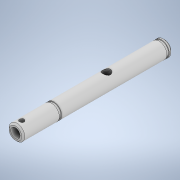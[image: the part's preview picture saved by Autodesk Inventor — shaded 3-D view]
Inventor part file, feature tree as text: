
AUTODESK INVENTOR PART (.ipt)
format: ipt  version: 2022 (Build 260153000, 153)  size: 167,936 bytes
history: native  units: mm
features: sketch x4, extrude x3, thread x2, projected_geometry x2, revolve x1, plane x1
ambient origin geometry x8: Origin, YZ Plane, XZ Plane, XY Plane, X Axis, Y Axis, Z Axis, Center Point
bodies: Solid1 (feature_tree)
feature tree (13):
  revolve  "Revolution1"  [1 undecoded]
  extrude  "Extrusion1"  Depth=1.5mm
  plane  "Work Plane1"
  extrude  "Extrusion2"  Depth=1.5mm
  extrude  "Extrusion3"  TaperAngle=135.0deg  [1 undecoded]
  thread  "Thread1"  [1 undecoded]
  thread  "Thread2"  [1 undecoded]
  sketch  "Sketch1"  dims[d9=95.0mm d10=5.0mm]
  sketch  "Sketch2"  dims[d11=0.5mm d12=1.5mm]
  sketch  "Sketch3"  dims[d13=1.5mm d14=2.0mm]
  projected_geometry  "Projected Loop1"
  sketch  "Sketch4"  dims[d15=1.0mm d16=135.0deg d17=67.0mm d18=135.0deg d19=1.414mm d20=90.0deg d21=6.0mm d22=10.0mm d23=0.0mm d24=5.0mm d25=5.0mm d26=67.0mm d27=33.5mm d28=10.0mm d29=0.0mm d30=3.0mm d31=4.0mm d32=10.0mm d33=0.0mm d34=10.0mm d35=0.0mm d36=10.0mm d37=0.0mm]
  projected_geometry  "Projected Loop2"
note: 4 required parameter values undecoded (feature->parameter linkage not recoverable at this tier; creation-order binding heuristic only, values carry confidence <= 0.55)